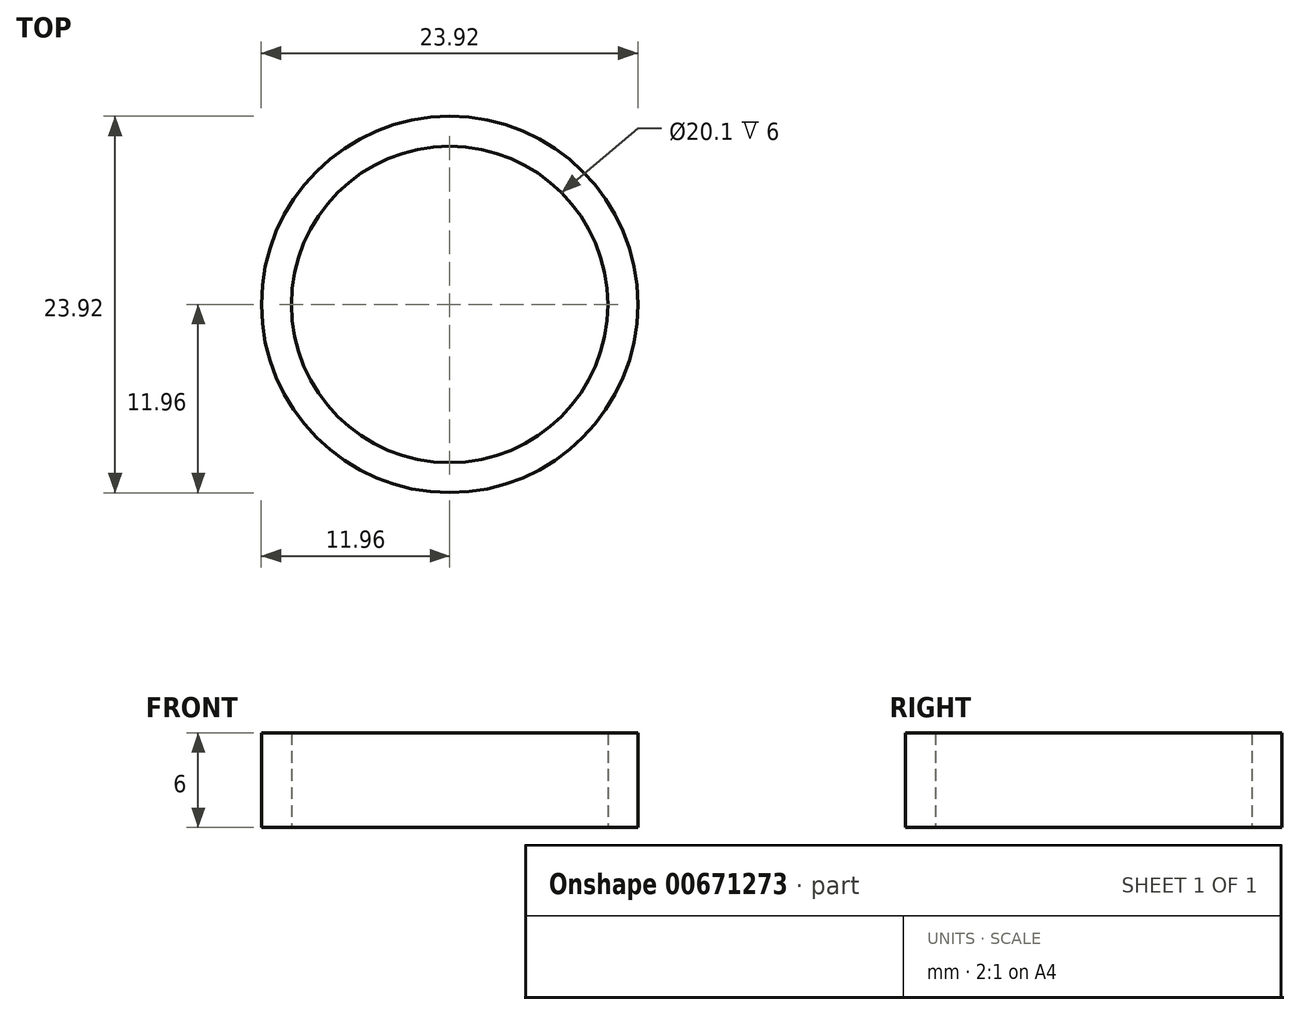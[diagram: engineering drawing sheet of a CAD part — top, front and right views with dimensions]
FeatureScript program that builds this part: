
annotation { "Feature Type Name" : "Feature", "Feature Type Description" : "" }
export const myFeature = defineFeature(function(context is Context, id is Id, definition is map)
    precondition{}
    {
        {
            var Q0;
            Q0=qCreatedBy(makeId("Top.planeOp"),FACE);
            var sketch = newSketch(context, id + "F0", { "sketchPlane" : qUnion([Q0])});
            skCircle(sketch, "E0", {"center": v(0, 0) * mm, "radius": 10.05 * mm});
            skCircle(sketch, "E1", {"center": v(0, 0) * mm, "radius": 11.95 * mm});
            skSolve(sketch);
        }
        {
            var Q0;
            Q0=makeQuery(id+"F0.imprint","IMPRINT",FACE,{"disambiguationData":[TD([[makeQuery(id+"F0.imprint","IMPRINT",EDGE,{"derivedFrom":sQuery(id+"F0.wireOp",EDGE,"E0")}),-1.0]])]});
            extrude(context, id + "F1", {"entities" : qUnion([Q0]), "depth" : 6 * mm, "offsetDistance" : 25.4 * mm});
        }
    });
